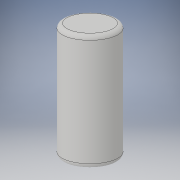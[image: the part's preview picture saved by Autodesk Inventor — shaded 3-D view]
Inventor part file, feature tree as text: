
AUTODESK INVENTOR PART (.ipt)
format: ipt  version: 2018 (Build 220112000, 112)  size: 105,472 bytes
history: native  units: mm
features: extrude x1, fillet x1, sketch x1
ambient origin geometry x8: Origin, YZ Plane, XZ Plane, XY Plane, X Axis, Y Axis, Z Axis, Center Point
bodies: Solid1 (feature_tree)
feature tree (3):
  extrude  "Extrusion1"  Depth=13.0mm TaperAngle=0.0deg
  fillet  "Fillet1"  Radius=0.5mm
  sketch  "Sketch1"  dims[d0=6.0mm d1=13.0mm d2=0.0mm d3=0.5mm]
